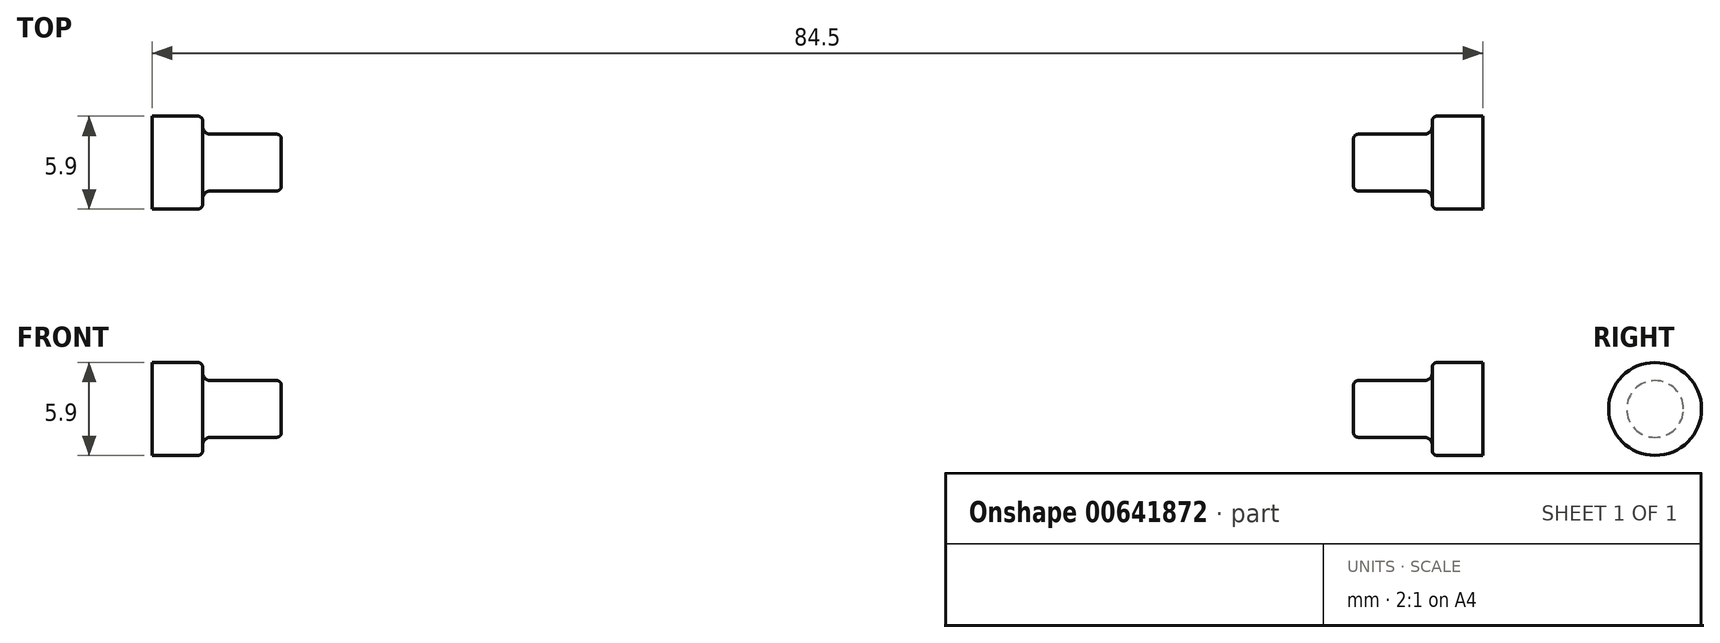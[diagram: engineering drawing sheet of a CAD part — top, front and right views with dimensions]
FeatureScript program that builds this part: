
annotation { "Feature Type Name" : "Feature", "Feature Type Description" : "" }
export const myFeature = defineFeature(function(context is Context, id is Id, definition is map)
    precondition{}
    {
        {
            var Q0;
            Q0=qCreatedBy(makeId("Front.planeOp"),FACE);
            var sketch = newSketch(context, id + "F0", { "sketchPlane" : qUnion([Q0])});
            skLineSegment(sketch, "E0.bottom", {"start": v(-34.05, 3.5) * mm, "end": v(34.05, 3.5) * mm});
            skLineSegment(sketch, "E0.top", {"start": v(-34.05, -3.5) * mm, "end": v(34.05, -3.5) * mm});
            skLineSegment(sketch, "E0.left", {"start": v(-34.05, 3.5) * mm, "end": v(-34.05, -3.5) * mm});
            skLineSegment(sketch, "E0.right", {"start": v(34.05, 3.5) * mm, "end": v(34.05, -3.5) * mm});
            skLineSegment(sketch, "E1.top", {"start": v(-34.05, 1.8) * mm, "end": v(-39.05, 1.8) * mm});
            skLineSegment(sketch, "E1.left", {"start": v(-34.05, 1.8) * mm, "end": v(-34.05, 0) * mm});
            skLineSegment(sketch, "E1.right", {"start": v(-39.05, 1.8) * mm, "end": v(-39.05, 0) * mm});
            skLineSegment(sketch, "E2.bottom", {"start": v(-42.25, 2.95) * mm, "end": v(-39.05, 2.95) * mm});
            skLineSegment(sketch, "E2.top", {"start": v(-42.25, -2.95) * mm, "end": v(-39.05, -2.95) * mm});
            skLineSegment(sketch, "E2.left", {"start": v(-42.25, 2.95) * mm, "end": v(-42.25, -2.95) * mm});
            skLineSegment(sketch, "E2.right", {"start": v(-39.05, 2.95) * mm, "end": v(-39.05, -2.95) * mm});
            skLineSegment(sketch, "E3.bottom", {"start": v(34.05, -1.8) * mm, "end": v(39.05, -1.8) * mm});
            skLineSegment(sketch, "E3.top", {"start": v(34.05, 1.8) * mm, "end": v(39.05, 1.8) * mm});
            skLineSegment(sketch, "E3.left", {"start": v(34.05, 1.8) * mm, "end": v(34.05, -1.8) * mm});
            skLineSegment(sketch, "E3.right", {"start": v(39.05, 1.8) * mm, "end": v(39.05, -1.8) * mm});
            skLineSegment(sketch, "E4.bottom", {"start": v(39.05, 2.95) * mm, "end": v(42.25, 2.95) * mm});
            skLineSegment(sketch, "E4.top", {"start": v(39.05, -2.95) * mm, "end": v(42.25, -2.95) * mm});
            skLineSegment(sketch, "E4.left", {"start": v(39.05, 2.95) * mm, "end": v(39.05, -2.95) * mm});
            skLineSegment(sketch, "E4.right", {"start": v(42.25, 2.95) * mm, "end": v(42.25, -2.95) * mm});
            skLineSegment(sketch, "E5", {"start": v(-42.25, 0) * mm, "end": v(42.25, 0) * mm});
            skLineSegment(sketch, "E6", {"start": v(-39.05, -1.8) * mm, "end": v(-34.05, -1.8) * mm});
            skLineSegment(sketch, "E7.top", {"start": v(4.25, 3) * mm, "end": v(5.25, 3) * mm});
            skLineSegment(sketch, "E7.left", {"start": v(4.25, 3.5) * mm, "end": v(4.25, 3) * mm});
            skLineSegment(sketch, "E7.right", {"start": v(5.25, 3.5) * mm, "end": v(5.25, 3) * mm});
            skLineSegment(sketch, "E8.bottom", {"start": v(4.25, -3.5) * mm, "end": v(5.25, -3.5) * mm});
            skLineSegment(sketch, "E8.top", {"start": v(4.25, -3) * mm, "end": v(5.25, -3) * mm});
            skLineSegment(sketch, "E8.left", {"start": v(4.25, -3.5) * mm, "end": v(4.25, -3) * mm});
            skLineSegment(sketch, "E8.right", {"start": v(5.25, -3.5) * mm, "end": v(5.25, -3) * mm});
            skPoint(sketch, "E9", {"position": v(34.05, 0) * mm});
            skSolve(sketch);
        }
        {
            var Q0;
            {var subQ7=sQuery(id+"F0.wireOp",EDGE,"E1.left");Q0=makeQuery(id+"F0.imprint","IMPRINT",FACE,{"disambiguationData":[TD([[makeQuery(id+"F0.imprint","IMPRINT",EDGE,{"derivedFrom":subQ7}),1.0]])]});}
            var Q1;
            {var subQ0=sQuery(id+"F0.wireOp",EDGE,"E1.top");Q1=makeQuery(id+"F0.imprint","IMPRINT",FACE,{"disambiguationData":[TD([[makeQuery(id+"F0.imprint","IMPRINT",EDGE,{"derivedFrom":subQ0}),1.0]])]});}
            var Q2;
            {var subQ4=sQuery(id+"F0.wireOp",EDGE,"E2.bottom");Q2=makeQuery(id+"F0.imprint","IMPRINT",FACE,{"disambiguationData":[TD([[makeQuery(id+"F0.imprint","IMPRINT",EDGE,{"derivedFrom":subQ4}),-1.0]])]});}
            var Q3;
            {var subQ0=sQuery(id+"F0.wireOp",EDGE,"E3.top");Q3=makeQuery(id+"F0.imprint","IMPRINT",FACE,{"disambiguationData":[TD([[makeQuery(id+"F0.imprint","IMPRINT",EDGE,{"derivedFrom":subQ0}),-1.0]])]});}
            var Q4;
            {var subQ1=sQuery(id+"F0.wireOp",EDGE,"E4.bottom");Q4=makeQuery(id+"F0.imprint","IMPRINT",FACE,{"disambiguationData":[TD([[makeQuery(id+"F0.imprint","IMPRINT",EDGE,{"derivedFrom":subQ1}),-1.0]])]});}
            var Q5;
            Q5=sQuery(id+"F0.wireOp",EDGE,"E5");
            revolve(context, id + "F1", {"entities" : qUnion([Q0, Q1, Q2, Q3, Q4]), "axis" : qUnion([Q5]), "revolveType" : RevolveType.FULL});
        }
        {
            var Q0;
            Q0=makeQuery(id+"F1.opRevolve","SWEPT_EDGE",EDGE,{"disambiguationData":[OSD([sQuery(id+"F0.wireOp",EDGE,"E1.top"),sQuery(id+"F0.wireOp",EDGE,"E2.right")])]});
            var Q1;
            Q1=makeQuery(id+"F1.opRevolve","SWEPT_EDGE",EDGE,{"disambiguationData":[OSD([sQuery(id+"F0.wireOp",EDGE,"E3.top"),sQuery(id+"F0.wireOp",EDGE,"E4.left")])]});
            fillet(context, id + "F2", {"entities" : qUnion([Q0, Q1]), "radius" : .5 * mm, "tangentPropagation" : true, "allowEdgeOverflow" : false});
        }
        {
            var Q0;
            Q0=makeQuery(id+"F1.opRevolve","SWEPT_EDGE",EDGE,{"disambiguationData":[OSD([sQuery(id+"F0.wireOp",EDGE,"E0.bottom"),sQuery(id+"F0.wireOp",EDGE,"E0.left")])]});
            var Q1;
            Q1=makeQuery(id+"F1.opRevolve","SWEPT_EDGE",EDGE,{"disambiguationData":[OSD([sQuery(id+"F0.wireOp",EDGE,"E0.bottom"),sQuery(id+"F0.wireOp",EDGE,"E0.right")])]});
            var Q2;
            Q2=makeQuery(id+"F1.opRevolve","SWEPT_EDGE",EDGE,{"disambiguationData":[OSD([sQuery(id+"F0.wireOp",EDGE,"E4.bottom"),sQuery(id+"F0.wireOp",EDGE,"E4.left")])]});
            var Q3;
            Q3=makeQuery(id+"F1.opRevolve","SWEPT_EDGE",EDGE,{"disambiguationData":[OSD([sQuery(id+"F0.wireOp",EDGE,"E2.bottom"),sQuery(id+"F0.wireOp",EDGE,"E2.right")])]});
            fillet(context, id + "F3", {"entities" : qUnion([Q0, Q1, Q2, Q3]), "radius" : .3 * mm, "tangentPropagation" : true, "allowEdgeOverflow" : false});
        }
    });
